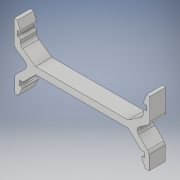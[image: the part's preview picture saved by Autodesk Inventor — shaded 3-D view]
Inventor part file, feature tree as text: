
AUTODESK INVENTOR PART (.ipt)
format: ipt  version: 2019 (Build 230136000, 136)  size: 201,728 bytes
history: native  units: mm
features: fillet x4, extrude x2, sketch x2, mirror x1
ambient origin geometry x8: Origin, YZ Plane, XZ Plane, XY Plane, X Axis, Y Axis, Z Axis, Center Point
bodies: Solid1 (feature_tree)
feature tree (9):
  extrude  "Extrusion1"  Depth=2.0mm
  mirror  "Mirror1"
  extrude  "Extrusion2"  Depth=54.0mm
  fillet  "Fillet1"  Radius=7.0mm
  fillet  "Fillet2"  Radius=3.0mm
  fillet  "Fillet3"  Radius=40.0mm
  fillet  "Fillet4"  Radius=1.5mm
  sketch  "Sketch1"  dims[d0=2.0mm d1=2.0mm]
  sketch  "Sketch2"  dims[d2=56.0mm d3=54.0mm d4=7.0mm d6=3.0mm d7=40.0mm d8=1.5mm d9=1.5mm d10=1.5mm d11=1.5mm d13=2.0mm d14=1.5mm d16=4.0mm d17=4.0mm d18=1.5mm d19=7.0mm d20=0.0mm d21=1.0mm d22=0.0mm d23=2.0mm d24=1.0mm d25=0.5mm d26=3.0mm d28=15.0mm d29=2.0mm]
